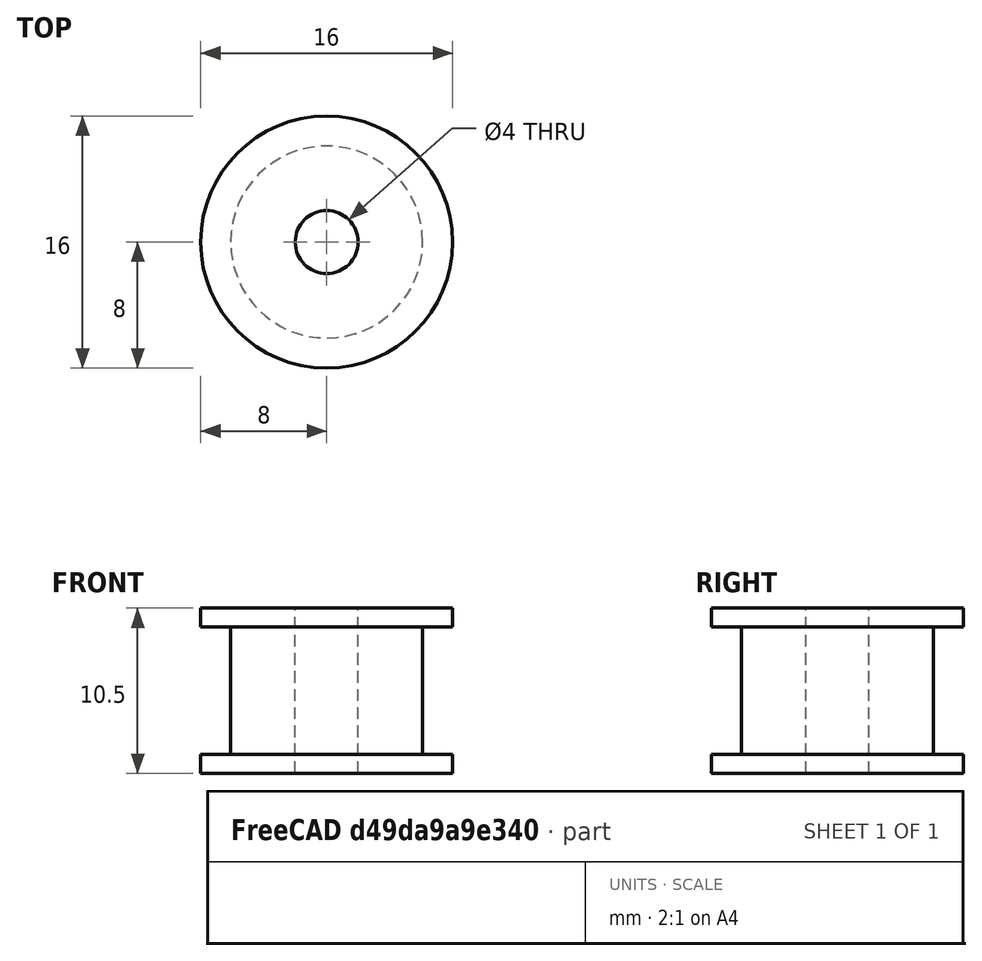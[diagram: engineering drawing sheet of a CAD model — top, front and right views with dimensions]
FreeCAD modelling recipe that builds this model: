
FCSTD DOCUMENT  (FreeCAD 1.0R38641 +468 (Git))
Label: cad_powge_pulley
License: All rights reserved
LicenseURL: https://en.wikipedia.org/wiki/All_rights_reserved
objects: Sketcher::SketchObject×1, PartDesign::Revolution×1, PartDesign::Body×1, App::Part×1
note: 6 computed .brp shape members not serialized (recipe doc carries the construction recipe); baked Part::Feature solids carry a one-line shape summary decoded from their .brp

FEATURE [Sketcher::SketchObject] Sketch
  ArcFitTolerance = 1e-06
  AttachmentSupport = -> [XZ_Plane]
  FullyConstrained = true
  MakeInternals = false
  MapMode = 5
  Placement = pos=(0,0,0) rot=(1,0,0;1.5708rad)
  sketch-geometry (8):
    g0: LineSegment StartX=6.1 StartY=9.3 StartZ=0 EndX=6.1 EndY=1.2 EndZ=0
    g1: LineSegment StartX=6.1 StartY=1.2 StartZ=0 EndX=8 EndY=1.2 EndZ=0
    g2: LineSegment StartX=8 StartY=1.2 StartZ=0 EndX=8 EndY=0 EndZ=0
    g3: LineSegment StartX=8 StartY=0 StartZ=0 EndX=2 EndY=0 EndZ=0
    g4: LineSegment StartX=2 StartY=0 StartZ=0 EndX=2 EndY=10.5 EndZ=0
    g5: LineSegment StartX=2 StartY=10.5 StartZ=0 EndX=8 EndY=10.5 EndZ=0
    g6: LineSegment StartX=8 StartY=10.5 StartZ=0 EndX=8 EndY=9.3 EndZ=0
    g7: LineSegment StartX=8 StartY=9.3 StartZ=0 EndX=6.1 EndY=9.3 EndZ=0
  constraints (24):
    c: Vertical(g0)
    c: Coincident(g1,g0)
    c: Horizontal(g1)
    c: Coincident(g2,g1)
    c: PointOnObject(g2,g-1)
    c: Vertical(g2)
    c: Coincident(g3,g2)
    c: PointOnObject(g3,g-1)
    c: Coincident(g4,g3)
    c: Vertical(g4)
    c: Coincident(g5,g4)
    c: Horizontal(g5)
    c: Coincident(g6,g5)
    c: Vertical(g6)
    c: Coincident(g7,g6)
    c: Horizontal(g7)
    c: Coincident(g0,g7)
    c: Equal(g5,g3)
    c: Equal(g6,g2)
    c: Distance(g4,g-2) = 2
    c: Distance(g5,g-2) = 8
    c: DistanceY(g0,g0) = 8.1
    c: DistanceY(g4,g4) = 10.5
    c: Distance(g0,g-2) = 6.1
FEATURE [PartDesign::Revolution] Revolution
  Angle = 360
  Angle2 = 60
  Axis = (0,2e-16,1)
  Base = (0,0,0)
  Placement = pos=(0,0,0) rot=(1,0,0;1.5708rad)
  Profile = -> Sketch
  ReferenceAxis = -> Sketch [V_Axis]
  Refine = true
  Reversed = true
  Suppressed = false
  Type = 0
FEATURE [PartDesign::Body] Body  label="powge_pulley"
  AllowCompound = false
  Group = -> [Sketch,Revolution]
  Origin = -> Origin
  Tip = -> Revolution
FEATURE [App::Part] Part  label="powge_pulley_part"
  Group = -> [Body]
  Origin = -> Origin001
